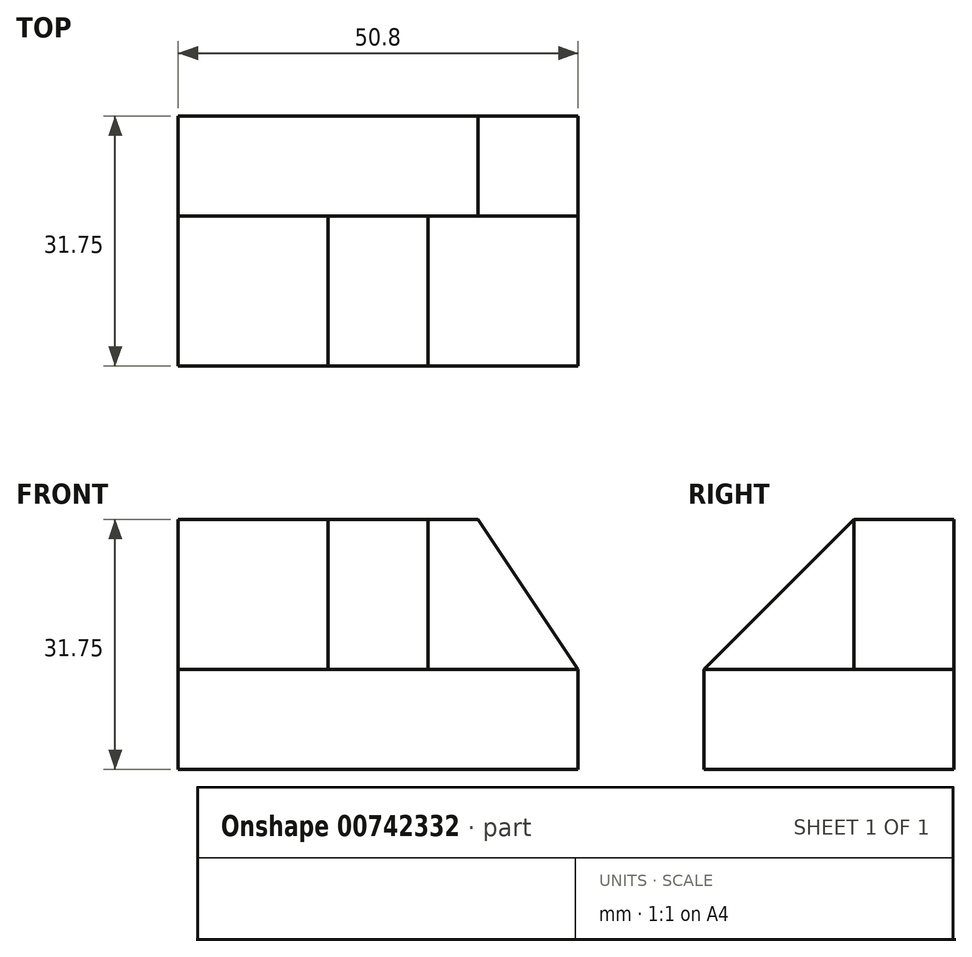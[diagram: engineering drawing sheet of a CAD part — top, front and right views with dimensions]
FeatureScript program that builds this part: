
annotation { "Feature Type Name" : "Feature", "Feature Type Description" : "" }
export const myFeature = defineFeature(function(context is Context, id is Id, definition is map)
    precondition{}
    {
        {
            var Q0;
            Q0=qCreatedBy(makeId("Front.planeOp"),FACE);
            var sketch = newSketch(context, id + "F0", { "sketchPlane" : qUnion([Q0])});
            skLineSegment(sketch, "E0", {"start": v(0, 0) * mm, "end": v(50.8, 0) * mm});
            skLineSegment(sketch, "E1", {"start": v(50.8, 0) * mm, "end": v(50.8, 31.75) * mm});
            skLineSegment(sketch, "E2", {"start": v(50.8, 31.75) * mm, "end": v(0, 31.75) * mm});
            skLineSegment(sketch, "E3", {"start": v(0, 31.75) * mm, "end": v(0, 0) * mm});
            skSolve(sketch);
        }
        {
            var Q0;
            Q0 = qSketchRegion(id + "F0", true);
            extrude(context, id + "F1", {"entities" : qUnion([Q0]), "depth" : 31.75 * mm, "offsetDistance" : 25.4 * mm});
        }
        {
            var Q0;
            Q0=makeQuery(id+"F1.opExtrude","CAP_FACE",FACE,{"disambiguationData":[OSD([sQuery(id+"F0.wireOp",EDGE,"E0"),sQuery(id+"F0.wireOp",EDGE,"E1"),sQuery(id+"F0.wireOp",EDGE,"E2"),sQuery(id+"F0.wireOp",EDGE,"E3")])],"isStart":false});
            var sketch = newSketch(context, id + "F2", { "sketchPlane" : qUnion([Q0])});
            skLineSegment(sketch, "E4", {"start": v(19.05, 31.75) * mm, "end": v(19.05, 12.7) * mm});
            skLineSegment(sketch, "E5", {"start": v(19.05, 12.7) * mm, "end": v(0, 12.7) * mm});
            skLineSegment(sketch, "E6", {"start": v(31.75, 31.75) * mm, "end": v(31.75, 12.7) * mm});
            skPoint(sketch, "E6.endSnap0", {"position": v(9.52, 12.7) * mm});
            skLineSegment(sketch, "E7", {"start": v(31.75, 12.7) * mm, "end": v(50.8, 12.7) * mm});
            skSolve(sketch);
        }
        {
            var Q0;
            Q0 = qSketchRegion(id + "F2", true);
            var Q1;
            {var subQ0=sQuery(id+"F2.wireOp",EDGE,"E4");Q1=makeQuery(id+"F2.imprint","IMPRINT",FACE,{"disambiguationData":[TD([[makeQuery(id+"F2.imprint","IMPRINT",EDGE,{"derivedFrom":subQ0}),-1.0]])]});}
            var Q2;
            {var subQ0=sQuery(id+"F2.wireOp",EDGE,"E6");Q2=makeQuery(id+"F2.imprint","IMPRINT",FACE,{"disambiguationData":[TD([[makeQuery(id+"F2.imprint","IMPRINT",EDGE,{"derivedFrom":subQ0}),1.0]])]});}
            extrude(context, id + "F3", {"entities" : qUnion([Q0, Q1, Q2]), "operationType" : NewBodyOperationType.REMOVE, "oppositeDirection" : true, "depth" : 19.05 * mm, "offsetDistance" : 25.4 * mm});
        }
        {
            var Q0;
            Q0=makeQuery(id+"F3.boolean.opBoolean","COPY",FACE,{"derivedFrom":makeQuery(id+"F3.opExtrude","SWEPT_FACE",FACE,{"disambiguationData":[OSD([sQuery(id+"F2.wireOp",EDGE,"E6")])]})});
            var sketch = newSketch(context, id + "F4", { "sketchPlane" : qUnion([Q0])});
            skLineSegment(sketch, "E8", {"start": v(-12.7, 31.75) * mm, "end": v(-31.75, 12.7) * mm});
            skSolve(sketch);
        }
        {
            var Q0;
            Q0 = qSketchRegion(id + "F4", true);
            var Q1;
            Q1=makeQuery(id+"F4.imprint","IMPRINT",FACE,{"disambiguationData":[TD([[makeQuery(id+"F4.imprint","IMPRINT",EDGE,{"derivedFrom":sQuery(id+"F4.wireOp",EDGE,"E8")}),-1.0]])]});
            extrude(context, id + "F5", {"entities" : qUnion([Q0, Q1]), "operationType" : NewBodyOperationType.REMOVE, "endBound" : BoundingType.THROUGH_ALL, "oppositeDirection" : true, "depth" : 25.4 * mm, "offsetDistance" : 25.4 * mm});
        }
        {
            var Q0;
            Q0=makeQuery(id+"F3.boolean.opBoolean","COPY",FACE,{"derivedFrom":makeQuery(id+"F3.opExtrude","CAP_FACE",FACE,{"disambiguationData":[OSD([sQuery(id+"F0.wireOp",EDGE,"E1"),sQuery(id+"F0.wireOp",EDGE,"E2"),sQuery(id+"F2.wireOp",EDGE,"E6"),sQuery(id+"F2.wireOp",EDGE,"E7")])],"isStart":false})});
            var sketch = newSketch(context, id + "F6", { "sketchPlane" : qUnion([Q0])});
            skLineSegment(sketch, "E9", {"start": v(38.1, 31.75) * mm, "end": v(50.8, 12.7) * mm});
            skSolve(sketch);
        }
        {
            var Q0;
            Q0 = qSketchRegion(id + "F6", true);
            var Q1;
            {var subQ0=sQuery(id+"F6.wireOp",EDGE,"E9");Q1=makeQuery(id+"F6.imprint","IMPRINT",FACE,{"disambiguationData":[TD([[makeQuery(id+"F6.imprint","IMPRINT",EDGE,{"derivedFrom":subQ0}),1.0]])]});}
            extrude(context, id + "F7", {"entities" : qUnion([Q0, Q1]), "operationType" : NewBodyOperationType.REMOVE, "endBound" : BoundingType.THROUGH_ALL, "oppositeDirection" : true, "depth" : 25.4 * mm, "offsetDistance" : 25.4 * mm});
        }
    });
